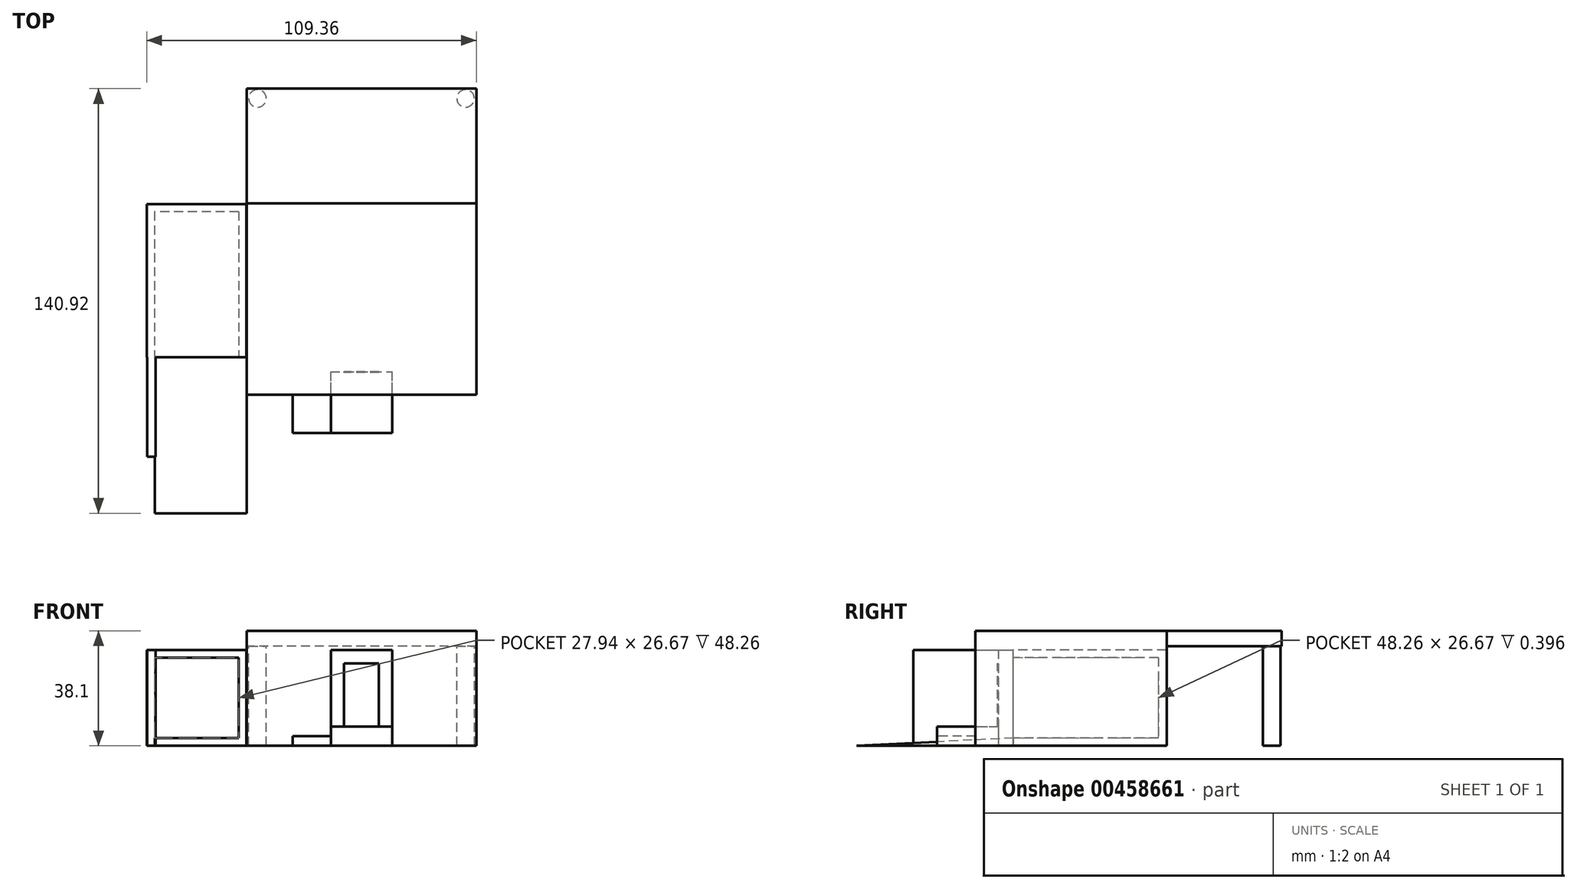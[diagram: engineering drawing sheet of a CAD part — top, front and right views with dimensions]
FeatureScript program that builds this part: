
annotation { "Feature Type Name" : "Feature", "Feature Type Description" : "" }
export const myFeature = defineFeature(function(context is Context, id is Id, definition is map)
    precondition{}
    {
        {
            var Q0;
            Q0=qCreatedBy(makeId("Top.planeOp"),FACE);
            var sketch = newSketch(context, id + "F0", { "sketchPlane" : qUnion([Q0])});
            skLineSegment(sketch, "E0.bottom", {"start": v(-10.16, -31.75) * mm, "end": v(-38.1, -31.75) * mm});
            skLineSegment(sketch, "E0.top", {"start": v(38.1, 31.75) * mm, "end": v(-38.1, 31.75) * mm});
            skLineSegment(sketch, "E0.left", {"start": v(38.1, -31.75) * mm, "end": v(38.1, 31.75) * mm});
            skLineSegment(sketch, "E0.right", {"start": v(-38.1, -31.75) * mm, "end": v(-38.1, -19.05) * mm});
            skPoint(sketch, "E0.middle", {"position": v(0, 0) * mm});
            skLineSegment(sketch, "E1.left", {"start": v(-38.1, 31.75) * mm, "end": v(-38.1, -19.05) * mm});
            skLineSegment(sketch, "E2", {"start": v(38.1, -31.75) * mm, "end": v(10.16, -31.75) * mm});
            skLineSegment(sketch, "E3.left", {"start": v(-10.16, -31.75) * mm, "end": v(-10.16, -31.75) * mm});
            skLineSegment(sketch, "E3.right", {"start": v(10.16, -31.75) * mm, "end": v(10.16, -31.75) * mm});
            skLineSegment(sketch, "E4.bottom", {"start": v(-10.16, -31.75) * mm, "end": v(10.16, -31.75) * mm});
            skLineSegment(sketch, "E4.top", {"start": v(-10.16, -24.13) * mm, "end": v(10.16, -24.13) * mm});
            skLineSegment(sketch, "E4.left", {"start": v(-10.16, -31.75) * mm, "end": v(-10.16, -24.13) * mm});
            skLineSegment(sketch, "E4.right", {"start": v(10.16, -31.75) * mm, "end": v(10.16, -24.13) * mm});
            skSolve(sketch);
        }
        {
            var Q0;
            Q0=makeQuery(id+"F0.imprint","IMPRINT",FACE,{"disambiguationData":[TD([[makeQuery(id+"F0.imprint","IMPRINT",EDGE,{"derivedFrom":sQuery(id+"F0.wireOp",EDGE,"E0.bottom")}),-1.0]])]});
            extrude(context, id + "F1", {"entities" : qUnion([Q0]), "depth" : 38.1 * mm});
        }
        {
            var Q0;
            Q0=makeQuery(id+"FcEcHTawdMJsb1V_0.boolean.opBoolean","MERGE",FACE,{"derivedFrom":[makeQuery(id+"F1.opExtrude","SWEPT_FACE",FACE,{"disambiguationData":[OSD([sQuery(id+"F0.wireOp",EDGE,"E0.top")])]}),makeQuery(id+"FcEcHTawdMJsb1V_0.opExtrude","SWEPT_FACE",FACE,{"disambiguationData":[OSD([sQuery(id+"F0.wireOp",EDGE,"E1.bottom")])]})]});
            var sketch = newSketch(context, id + "F2", { "sketchPlane" : qUnion([Q0])});
            skLineSegment(sketch, "E5.bottom", {"start": v(-38.1, 38.1) * mm, "end": v(38.1, 38.1) * mm});
            skLineSegment(sketch, "E5.top", {"start": v(-38.1, 33.02) * mm, "end": v(38.1, 33.02) * mm});
            skLineSegment(sketch, "E5.left", {"start": v(-38.1, 38.1) * mm, "end": v(-38.1, 33.02) * mm});
            skLineSegment(sketch, "E5.right", {"start": v(38.1, 38.1) * mm, "end": v(38.1, 33.02) * mm});
            skSolve(sketch);
        }
        {
            var Q0;
            Q0 = qSketchRegion(id + "F2", true);
            extrude(context, id + "F3", {"entities" : qUnion([Q0]), "depth" : 38.1 * mm});
        }
        {
            var Q0;
            Q0=makeQuery(id+"F3.opExtrude","SWEPT_FACE",FACE,{"disambiguationData":[OSD([sQuery(id+"F2.wireOp",EDGE,"E5.top")])]});
            var sketch = newSketch(context, id + "F4", { "sketchPlane" : qUnion([Q0])});
            skSolve(sketch);
        }
        {
            var Q0;
            Q0=makeQuery(id+"F1.opExtrude","SWEPT_FACE",FACE,{"disambiguationData":[OSD([sQuery(id+"F0.wireOp",EDGE,"E4.top")])]});
            var sketch = newSketch(context, id + "F5", { "sketchPlane" : qUnion([Q0])});
            skLineSegment(sketch, "E6.bottom", {"start": v(-10.16, 38.1) * mm, "end": v(10.16, 38.1) * mm});
            skLineSegment(sketch, "E6.top", {"start": v(-10.16, 31.75) * mm, "end": v(10.16, 31.75) * mm});
            skLineSegment(sketch, "E6.left", {"start": v(-10.16, 38.1) * mm, "end": v(-10.16, 31.75) * mm});
            skLineSegment(sketch, "E6.right", {"start": v(10.16, 38.1) * mm, "end": v(10.16, 31.75) * mm});
            skLineSegment(sketch, "E7.bottom", {"start": v(-10.16, 0) * mm, "end": v(10.16, 0) * mm});
            skLineSegment(sketch, "E7.top", {"start": v(-10.16, 6.35) * mm, "end": v(10.16, 6.35) * mm});
            skLineSegment(sketch, "E7.left", {"start": v(-10.16, 0) * mm, "end": v(-10.16, 6.35) * mm});
            skLineSegment(sketch, "E7.right", {"start": v(10.16, 0) * mm, "end": v(10.16, 6.35) * mm});
            skSolve(sketch);
        }
        {
            var Q0;
            Q0=makeQuery(id+"F5.imprint","IMPRINT",FACE,{"disambiguationData":[TD([[makeQuery(id+"F5.imprint","IMPRINT",EDGE,{"derivedFrom":sQuery(id+"F5.wireOp",EDGE,"E6.bottom")}),-1.0]])]});
            extrude(context, id + "F6", {"entities" : qUnion([Q0]), "operationType" : NewBodyOperationType.ADD, "depth" : 7.62 * mm});
        }
        {
            var Q0;
            Q0=makeQuery(id+"F3.boolean.opBoolean","MERGE",FACE,{"derivedFrom":[makeQuery(id+"F1.opExtrude","SWEPT_FACE",FACE,{"disambiguationData":[OSD([sQuery(id+"F0.wireOp",EDGE,"E0.right"),sQuery(id+"F0.wireOp",EDGE,"E1.left")])]}),makeQuery(id+"F3.opExtrude","SWEPT_FACE",FACE,{"disambiguationData":[OSD([sQuery(id+"F2.wireOp",EDGE,"E5.right")])]})]});
            var sketch = newSketch(context, id + "F7", { "sketchPlane" : qUnion([Q0])});
            skLineSegment(sketch, "E8", {"start": v(19.05, 2.54) * mm, "end": v(71.07, 0) * mm});
            skPoint(sketch, "E8.endSnap0", {"position": v(0, 0) * mm});
            skLineSegment(sketch, "E9", {"start": v(71.07, 0) * mm, "end": v(19.05, 0) * mm});
            skLineSegment(sketch, "E10", {"start": v(19.05, 0) * mm, "end": v(19.05, 2.54) * mm});
            skSolve(sketch);
        }
        {
            var Q0;
            Q0=qCreatedBy(makeId("Front.planeOp"),FACE);
            var sketch = newSketch(context, id + "F8", { "sketchPlane" : qUnion([Q0])});
            skLineSegment(sketch, "E11.bottom", {"start": v(-71.12, 31.75) * mm, "end": v(-68.33, 31.75) * mm});
            skLineSegment(sketch, "E11.top", {"start": v(-71.12, 0) * mm, "end": v(-68.33, 0) * mm});
            skLineSegment(sketch, "E11.left", {"start": v(-71.12, 31.75) * mm, "end": v(-71.12, 0) * mm});
            skLineSegment(sketch, "E11.right", {"start": v(-68.33, 31.75) * mm, "end": v(-68.33, 0) * mm});
            skSolve(sketch);
        }
        {
            var Q0;
            Q0 = qSketchRegion(id + "F8", true);
            extrude(context, id + "F9", {"entities" : qUnion([Q0]), "operationType" : NewBodyOperationType.ADD, "depth" : 52.32 * mm});
        }
        {
            var Q0;
            Q0=makeQuery(id+"F5.imprint","IMPRINT",FACE,{"disambiguationData":[TD([[makeQuery(id+"F5.imprint","IMPRINT",EDGE,{"derivedFrom":sQuery(id+"F5.wireOp",EDGE,"E7.bottom")}),1.0]])]});
            extrude(context, id + "F10", {"entities" : qUnion([Q0]), "depth" : 20.32 * mm});
        }
        {
            var Q0;
            Q0=makeQuery(id+"F10.opExtrude","SWEPT_FACE",FACE,{"disambiguationData":[OSD([sQuery(id+"F5.wireOp",EDGE,"E7.left")])]});
            var sketch = newSketch(context, id + "F11", { "sketchPlane" : qUnion([Q0])});
            skLineSegment(sketch, "E12.bottom", {"start": v(31.66, 0) * mm, "end": v(44.45, 0) * mm});
            skLineSegment(sketch, "E12.top", {"start": v(31.66, 3.18) * mm, "end": v(44.45, 3.18) * mm});
            skLineSegment(sketch, "E12.left", {"start": v(31.66, 0) * mm, "end": v(31.66, 3.18) * mm});
            skLineSegment(sketch, "E12.right", {"start": v(44.45, 0) * mm, "end": v(44.45, 3.18) * mm});
            skSolve(sketch);
        }
        {
            var Q0;
            Q0=makeQuery(id+"F11.imprint","IMPRINT",FACE,{"disambiguationData":[TD([[makeQuery(id+"F11.imprint","IMPRINT",EDGE,{"derivedFrom":sQuery(id+"F11.wireOp",EDGE,"E12.bottom")}),-1.0]])]});
            extrude(context, id + "F12", {"entities" : qUnion([Q0]), "depth" : 12.7 * mm});
        }
        {
            var Q0;
            {var subQ0=sQuery(id+"F5.wireOp",EDGE,"E6.top");Q0=makeQuery(id+"F5.imprint","IMPRINT",FACE,{"disambiguationData":[TD([[makeQuery(id+"F5.imprint","IMPRINT",EDGE,{"derivedFrom":subQ0}),-1.0]])]});}
            var sketch = newSketch(context, id + "F13", { "sketchPlane" : qUnion([Q0])});
            skLineSegment(sketch, "E13.bottom", {"start": v(5.8, 6.35) * mm, "end": v(0, 6.35) * mm});
            skLineSegment(sketch, "E13.top", {"start": v(5.8, 27.29) * mm, "end": v(0, 27.29) * mm});
            skLineSegment(sketch, "E13.left", {"start": v(0, 6.35) * mm, "end": v(0, 27.29) * mm});
            skLineSegment(sketch, "E13.right", {"start": v(5.8, 6.35) * mm, "end": v(5.8, 27.29) * mm});
            skLineSegment(sketch, "E14.MirrorCS", {"start": v(-5.8, 6.35) * mm, "end": v(-5.8, 27.29) * mm});
            skLineSegment(sketch, "E15.MirrorCS", {"start": v(-5.8, 27.29) * mm, "end": v(0, 27.29) * mm});
            skLineSegment(sketch, "E16.MirrorCS", {"start": v(-5.8, 6.35) * mm, "end": v(0, 6.35) * mm});
            skSolve(sketch);
        }
        {
            var Q0;
            Q0 = qSketchRegion(id + "F13", true);
            extrude(context, id + "F14", {"entities" : qUnion([Q0]), "depth" : 0.25 * mm});
        }
        {
            var Q0;
            Q0=qCreatedBy(makeId("Top.planeOp"),FACE);
            var sketch = newSketch(context, id + "F15", { "sketchPlane" : qUnion([Q0])});
            skLineSegment(sketch, "E17.bottom", {"start": v(-38.24, 31.54) * mm, "end": v(-71.26, 31.54) * mm});
            skLineSegment(sketch, "E17.top", {"start": v(-38.24, -19.26) * mm, "end": v(-71.26, -19.26) * mm});
            skLineSegment(sketch, "E17.left", {"start": v(-38.24, 31.54) * mm, "end": v(-38.24, -19.26) * mm});
            skLineSegment(sketch, "E17.right", {"start": v(-71.26, 31.54) * mm, "end": v(-71.26, -19.26) * mm});
            skSolve(sketch);
        }
        {
            var Q0;
            Q0=makeQuery(id+"F15.imprint","IMPRINT",FACE,{"disambiguationData":[TD([[makeQuery(id+"F15.imprint","IMPRINT",EDGE,{"derivedFrom":sQuery(id+"F15.wireOp",EDGE,"E17.bottom")}),1.0]])]});
            extrude(context, id + "F16", {"entities" : qUnion([Q0]), "operationType" : NewBodyOperationType.ADD, "depth" : 31.75 * mm});
        }
        {
            var Q0;
            {var subQ0=sQuery(id+"F7.wireOp",EDGE,"E10");Q0=makeQuery(id+"F7.imprint","IMPRINT",FACE,{"disambiguationData":[TD([[makeQuery(id+"F7.imprint","IMPRINT",EDGE,{"derivedFrom":subQ0}),-1.0]])]});}
            var Q1;
            {var subQ0=sQuery(id+"F7.wireOp",EDGE,"E9");var subQ1=sQuery(id+"F7.wireOp",EDGE,"E8");var subQ2=makeQuery(id+"F7.imprint","INTERSECT",VERTEX,{"derivedFrom":[subQ1,subQ0]});Q1=makeQuery(id+"F7.imprint","IMPRINT",FACE,{"disambiguationData":[TD([[makeQuery(id+"F7.imprint","IMPRINT",EDGE,{"disambiguationData":[TD([[subQ2,1.0]])],"derivedFrom":subQ1}),-1.0]])]});}
            extrude(context, id + "F17", {"entities" : qUnion([Q0, Q1]), "depth" : 30.48 * mm});
        }
        {
            var Q0;
            Q0=makeQuery(id+"F16.opExtrude","SWEPT_FACE",FACE,{"disambiguationData":[OSD([sQuery(id+"F15.wireOp",EDGE,"E17.top")])]});
            shell(context, id + "F18", {"entities" : qUnion([Q0]), "thickness" : 2.54 * mm});
        }
        {
            var Q0;
            {var subQ0=sQuery(id+"F2.wireOp",EDGE,"E5.top");Q0=makeQuery(id+"F4.imprint","IMPRINT",FACE,{"disambiguationData":[TD([[makeQuery(id+"F4.imprint","IMPRINT",EDGE,{"derivedFrom":makeQuery(id+"F3.opExtrude","CAP_EDGE",EDGE,{"disambiguationData":[OSD([subQ0])],"isStart":true})}),1.0]])]});}
            var sketch = newSketch(context, id + "F19", { "sketchPlane" : qUnion([Q0])});
            skCircle(sketch, "E18", {"center": v(34.51, -66.6) * mm, "radius": 2.91 * mm});
            skCircle(sketch, "E19.MirrorC", {"center": v(-34.51, -66.6) * mm, "radius": 2.91 * mm});
            skSolve(sketch);
        }
        {
            var Q0;
            Q0 = qSketchRegion(id + "F19", true);
            extrude(context, id + "F20", {"entities" : qUnion([Q0]), "depth" : 33.02 * mm});
        }
    });
